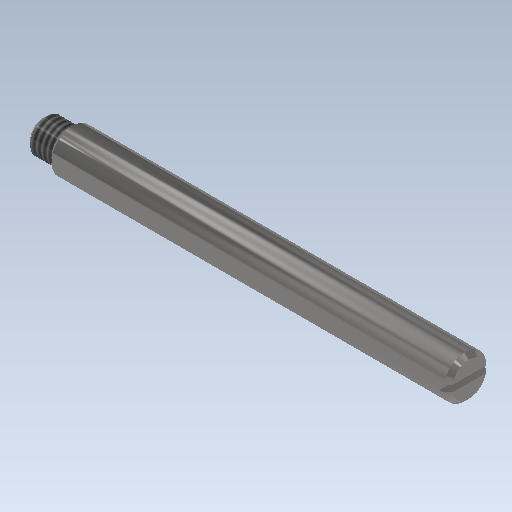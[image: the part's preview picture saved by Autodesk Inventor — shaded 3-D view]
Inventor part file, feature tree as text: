
AUTODESK INVENTOR PART (.ipt)
format: ipt  version: 2020.1 (Build 241239000, 239)  size: 136,192 bytes
history: native  units: mm
features: chamfer x2, sketch x2, revolve x1, thread x1, extrude x1
ambient origin geometry x8: Origin, YZ Plane, XZ Plane, XY Plane, X Axis, Y Axis, Z Axis, Center Point
bodies: Solid1 (feature_tree)
feature tree (7):
  revolve  "Revolution1"  [1 undecoded]
  thread  "Thread1"  [1 undecoded]
  chamfer  "Chamfer1"  Distance=10.0mm
  extrude  "Extrusion1"  Depth=10.0mm TaperAngle=45.0deg
  chamfer  "Chamfer2"  Distance=1.5mm
  sketch  "Sketch1"  dims[d0=8.0mm d1=10.0mm d3=100.0mm]
  sketch  "Sketch2"  dims[d4=90.0deg d5=10.0mm d6=0.0mm d7=1.0mm d8=2.0mm d9=45.0deg d10=1.5mm d11=2.0mm d12=10.0mm d13=0.0mm d14=1.0mm d15=2.0mm d16=45.0deg d17=7.0mm d18=1.0mm d19=7.0mm]
note: 2 required parameter values undecoded (feature->parameter linkage not recoverable at this tier; creation-order binding heuristic only, values carry confidence <= 0.55)